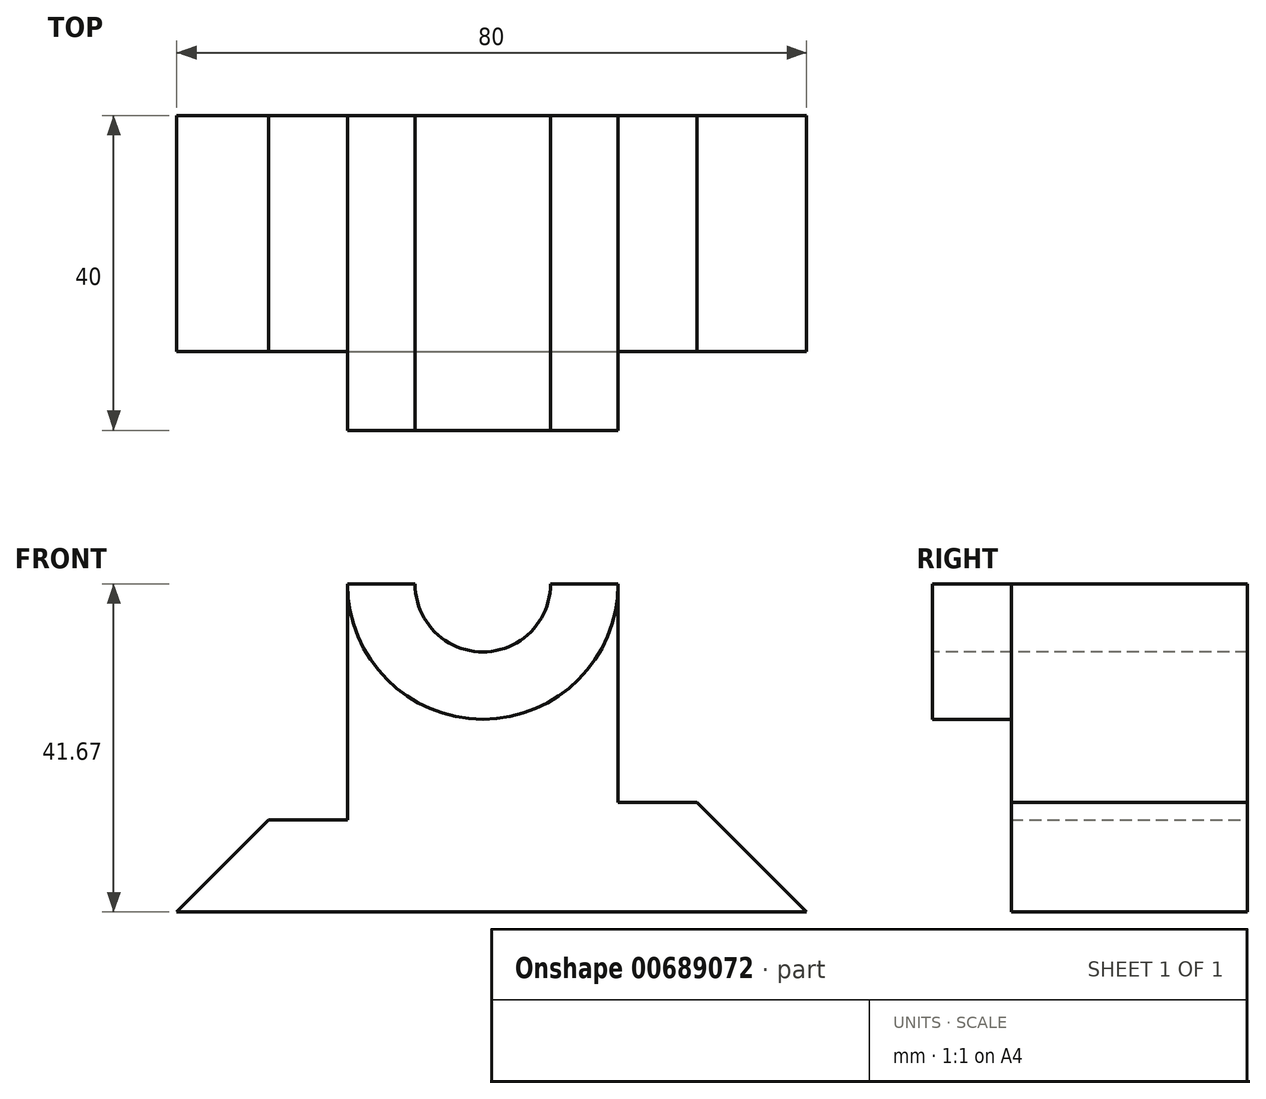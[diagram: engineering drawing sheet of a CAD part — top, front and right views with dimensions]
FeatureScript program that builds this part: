
annotation { "Feature Type Name" : "Feature", "Feature Type Description" : "" }
export const myFeature = defineFeature(function(context is Context, id is Id, definition is map)
    precondition{}
    {
        {
            var Q0;
            Q0=qCreatedBy(makeId("Front.planeOp"),FACE);
            var sketch = newSketch(context, id + "F0", { "sketchPlane" : qUnion([Q0])});
            skLineSegment(sketch, "E0", {"start": v(-43.52, -36.06) * mm, "end": v(36.48, -36.06) * mm});
            skLineSegment(sketch, "E1", {"start": v(36.48, -36.06) * mm, "end": v(22.54, -22.12) * mm});
            skLineSegment(sketch, "E2", {"start": v(22.54, -22.12) * mm, "end": v(12.54, -22.12) * mm});
            skLineSegment(sketch, "E3", {"start": v(12.54, -22.12) * mm, "end": v(12.54, 5.61) * mm});
            skLineSegment(sketch, "E4", {"start": v(12.54, 5.61) * mm, "end": v(-21.84, 5.61) * mm});
            skLineSegment(sketch, "E5", {"start": v(-21.84, 5.61) * mm, "end": v(-21.84, -24.39) * mm});
            skLineSegment(sketch, "E6", {"start": v(-21.84, -24.39) * mm, "end": v(-31.84, -24.39) * mm});
            skLineSegment(sketch, "E7", {"start": v(-31.84, -24.39) * mm, "end": v(-43.52, -36.06) * mm});
            skSolve(sketch);
        }
        {
            var Q0;
            Q0 = qSketchRegion(id + "F0", true);
            extrude(context, id + "F1", {"entities" : qUnion([Q0]), "depth" : 30 * mm, "offsetDistance" : 25.4 * mm});
        }
        {
            var Q0;
            Q0=makeQuery(id+"F1.opExtrude","CAP_FACE",FACE,{"disambiguationData":[OSD([sQuery(id+"F0.wireOp",EDGE,"E0"),sQuery(id+"F0.wireOp",EDGE,"E1"),sQuery(id+"F0.wireOp",EDGE,"E2"),sQuery(id+"F0.wireOp",EDGE,"E3"),sQuery(id+"F0.wireOp",EDGE,"E4"),sQuery(id+"F0.wireOp",EDGE,"E5"),sQuery(id+"F0.wireOp",EDGE,"E6"),sQuery(id+"F0.wireOp",EDGE,"E7")])],"isStart":false});
            var sketch = newSketch(context, id + "F2", { "sketchPlane" : qUnion([Q0])});
            skArc(sketch, "E8", {"start": v(-21.84, 5.61) * mm, "mid": v(-4.65, -11.58) * mm, "end": v(12.54, 5.61) * mm});
            skLineSegment(sketch, "E9", {"start": v(-21.84, 5.61) * mm, "end": v(12.54, 5.61) * mm});
            skSolve(sketch);
        }
        {
            var Q0;
            Q0 = qSketchRegion(id + "F2", true);
            extrude(context, id + "F3", {"entities" : qUnion([Q0]), "operationType" : NewBodyOperationType.ADD, "depth" : 10 * mm, "offsetDistance" : 25.4 * mm});
        }
        {
            var Q0;
            Q0=makeQuery(id+"F3.opExtrude","CAP_FACE",FACE,{"disambiguationData":[OSD([sQuery(id+"F2.wireOp",EDGE,"E8"),sQuery(id+"F2.wireOp",EDGE,"E9")])],"isStart":false});
            var sketch = newSketch(context, id + "F4", { "sketchPlane" : qUnion([Q0])});
            skLineSegment(sketch, "E10", {"start": v(-21.84, 5.61) * mm, "end": v(-4.65, 5.61) * mm});
            skLineSegment(sketch, "E11", {"start": v(-4.65, 5.61) * mm, "end": v(12.54, 5.61) * mm});
            skArc(sketch, "E12", {"start": v(-13.25, 5.61) * mm, "mid": v(-4.65, -3.02) * mm, "end": v(3.95, 5.61) * mm});
            skLineSegment(sketch, "E13", {"start": v(-13.25, 5.61) * mm, "end": v(3.95, 5.61) * mm});
            skSolve(sketch);
        }
        {
            var Q0;
            Q0=makeQuery(id+"F4.imprint","IMPRINT",FACE,{"disambiguationData":[TD([[makeQuery(id+"F4.imprint","IMPRINT",EDGE,{"derivedFrom":sQuery(id+"F4.wireOp",EDGE,"E12")}),1.0]])]});
            extrude(context, id + "F5", {"entities" : qUnion([Q0]), "operationType" : NewBodyOperationType.REMOVE, "oppositeDirection" : true, "depth" : 40 * mm, "offsetDistance" : 25.4 * mm});
        }
    });
